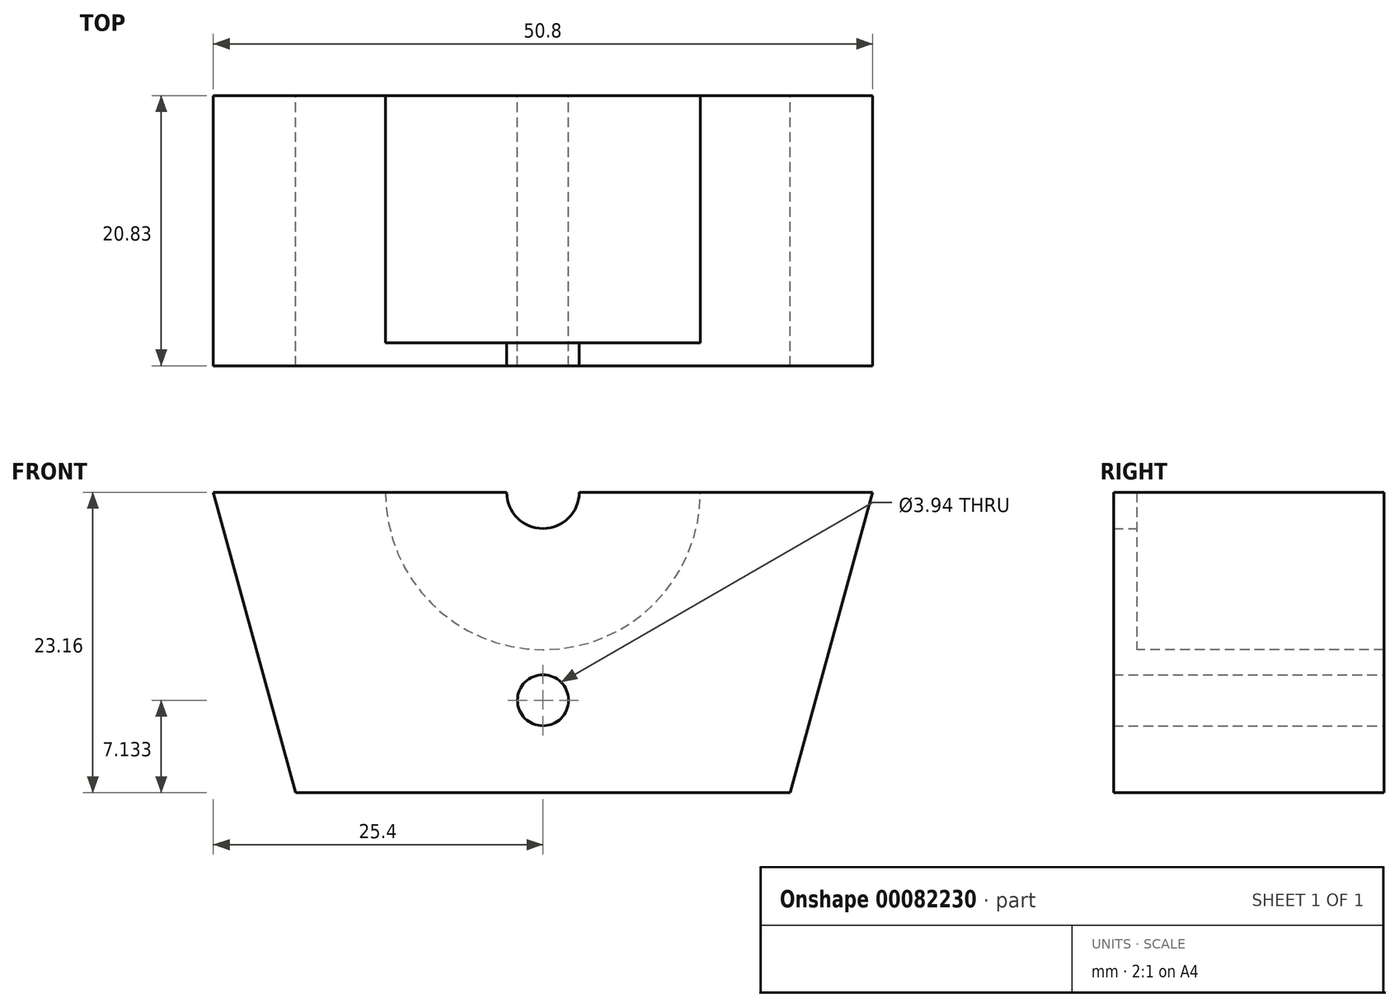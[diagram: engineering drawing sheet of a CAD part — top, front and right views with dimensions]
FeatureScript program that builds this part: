
annotation { "Feature Type Name" : "Feature", "Feature Type Description" : "" }
export const myFeature = defineFeature(function(context is Context, id is Id, definition is map)
    precondition{}
    {
        {
            var Q0;
            Q0=qCreatedBy(makeId("Front.planeOp"),FACE);
            var sketch = newSketch(context, id + "F0", { "sketchPlane" : qUnion([Q0])});
            skArc(sketch, "E0", {"start": v(-2.8, 0) * mm, "mid": v(0, -2.8) * mm, "end": v(2.8, 0) * mm});
            skCircle(sketch, "E1", {"center": v(0, -16.03) * mm, "radius": 1.97 * mm});
            skLineSegment(sketch, "E2", {"start": v(-2.8, 0) * mm, "end": v(-25.4, 0) * mm});
            skLineSegment(sketch, "E3", {"start": v(0, -23.16) * mm, "end": v(-19.05, -23.16) * mm});
            skLineSegment(sketch, "E4", {"start": v(-25.4, 0) * mm, "end": v(-19.05, -23.16) * mm});
            skLineSegment(sketch, "E5.MirrorCS", {"start": v(2.8, 0) * mm, "end": v(25.4, 0) * mm});
            skLineSegment(sketch, "E6.MirrorCS", {"start": v(25.4, 0) * mm, "end": v(19.05, -23.16) * mm});
            skLineSegment(sketch, "E7.MirrorCS", {"start": v(0, -23.16) * mm, "end": v(19.05, -23.16) * mm});
            skSolve(sketch);
        }
        {
            var Q0;
            Q0=makeQuery(id+"F0.imprint","IMPRINT",FACE,{"disambiguationData":[TD([[makeQuery(id+"F0.imprint","IMPRINT",EDGE,{"derivedFrom":sQuery(id+"F0.wireOp",EDGE,"E0")}),-1.0]])]});
            extrude(context, id + "F1", {"entities" : qUnion([Q0]), "depth" : 1.78 * mm});
        }
        {
            var Q0;
            Q0=makeQuery(id+"F1.opExtrude","CAP_FACE",FACE,{"disambiguationData":[OSD([sQuery(id+"F0.wireOp",EDGE,"E0"),sQuery(id+"F0.wireOp",EDGE,"E1"),sQuery(id+"F0.wireOp",EDGE,"E2"),sQuery(id+"F0.wireOp",EDGE,"E3"),sQuery(id+"F0.wireOp",EDGE,"E4"),sQuery(id+"F0.wireOp",EDGE,"E5.MirrorCS"),sQuery(id+"F0.wireOp",EDGE,"E6.MirrorCS"),sQuery(id+"F0.wireOp",EDGE,"E7.MirrorCS")])],"isStart":true});
            var sketch = newSketch(context, id + "F2", { "sketchPlane" : qUnion([Q0])});
            skArc(sketch, "E8", {"start": v(-12.13, 0) * mm, "mid": v(0, -12.13) * mm, "end": v(12.13, 0) * mm});
            skLineSegment(sketch, "E9.0", {"start": v(-12.13, 0) * mm, "end": v(-25.4, 0) * mm});
            skLineSegment(sketch, "E10.0", {"start": v(-25.4, 0) * mm, "end": v(-19.05, -23.16) * mm});
            skLineSegment(sketch, "E11.0", {"start": v(12.13, 0) * mm, "end": v(25.4, 0) * mm});
            skLineSegment(sketch, "E12.0", {"start": v(25.4, 0) * mm, "end": v(19.05, -23.16) * mm});
            skLineSegment(sketch, "E13.0", {"start": v(-19.05, -23.16) * mm, "end": v(19.05, -23.16) * mm});
            skCircle(sketch, "E14.0", {"center": v(0, -16.03) * mm, "radius": 1.97 * mm});
            skPoint(sketch, "E15.orphan", {"position": v(-2.8, 0) * mm});
            skPoint(sketch, "E16.orphan", {"position": v(2.8, 0) * mm});
            skSolve(sketch);
        }
        {
            var Q0;
            Q0 = qSketchRegion(id + "F2", true);
            extrude(context, id + "F3", {"entities" : qUnion([Q0]), "operationType" : NewBodyOperationType.ADD, "depth" : 19.05 * mm});
        }
    });
